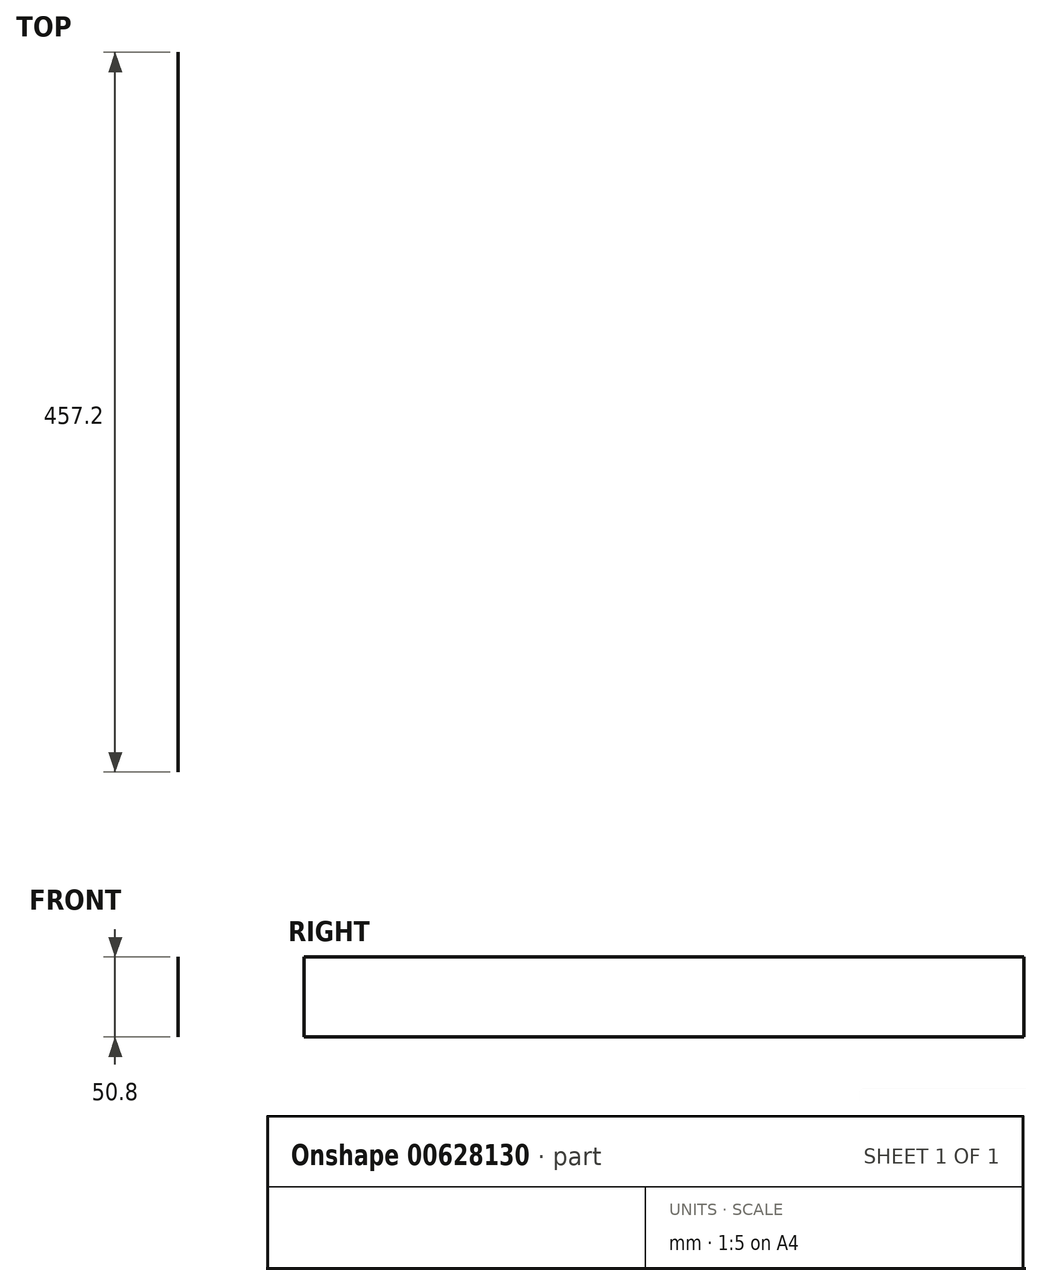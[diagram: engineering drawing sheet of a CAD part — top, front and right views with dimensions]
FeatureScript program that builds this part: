
annotation { "Feature Type Name" : "Feature", "Feature Type Description" : "" }
export const myFeature = defineFeature(function(context is Context, id is Id, definition is map)
    precondition{}
    {
        {
            var Q0;
            Q0=qCreatedBy(makeId("Top.planeOp"),FACE);
            var sketch = newSketch(context, id + "F0", { "sketchPlane" : qUnion([Q0])});
            skLineSegment(sketch, "E0.bottom", {"start": v(228.6, 228.6) * mm, "end": v(-228.6, 228.6) * mm});
            skLineSegment(sketch, "E0.top", {"start": v(228.6, -228.6) * mm, "end": v(-228.6, -228.6) * mm});
            skLineSegment(sketch, "E0.left", {"start": v(228.6, 228.6) * mm, "end": v(228.6, -228.6) * mm});
            skLineSegment(sketch, "E0.right", {"start": v(-228.6, 228.6) * mm, "end": v(-228.6, -228.6) * mm});
            skPoint(sketch, "E0.middle", {"position": v(0, 0) * mm});
            skSolve(sketch);
        }
        {
            var Q0;
            Q0=sQuery(id+"F0.wireOp",EDGE,"E0.left");
            extrude(context, id + "F1", {"bodyType" : ToolBodyType.SURFACE, "surfaceEntities" : qUnion([Q0]), "depth" : 50.8 * mm, "offsetDistance" : 25.4 * mm});
        }
    });
